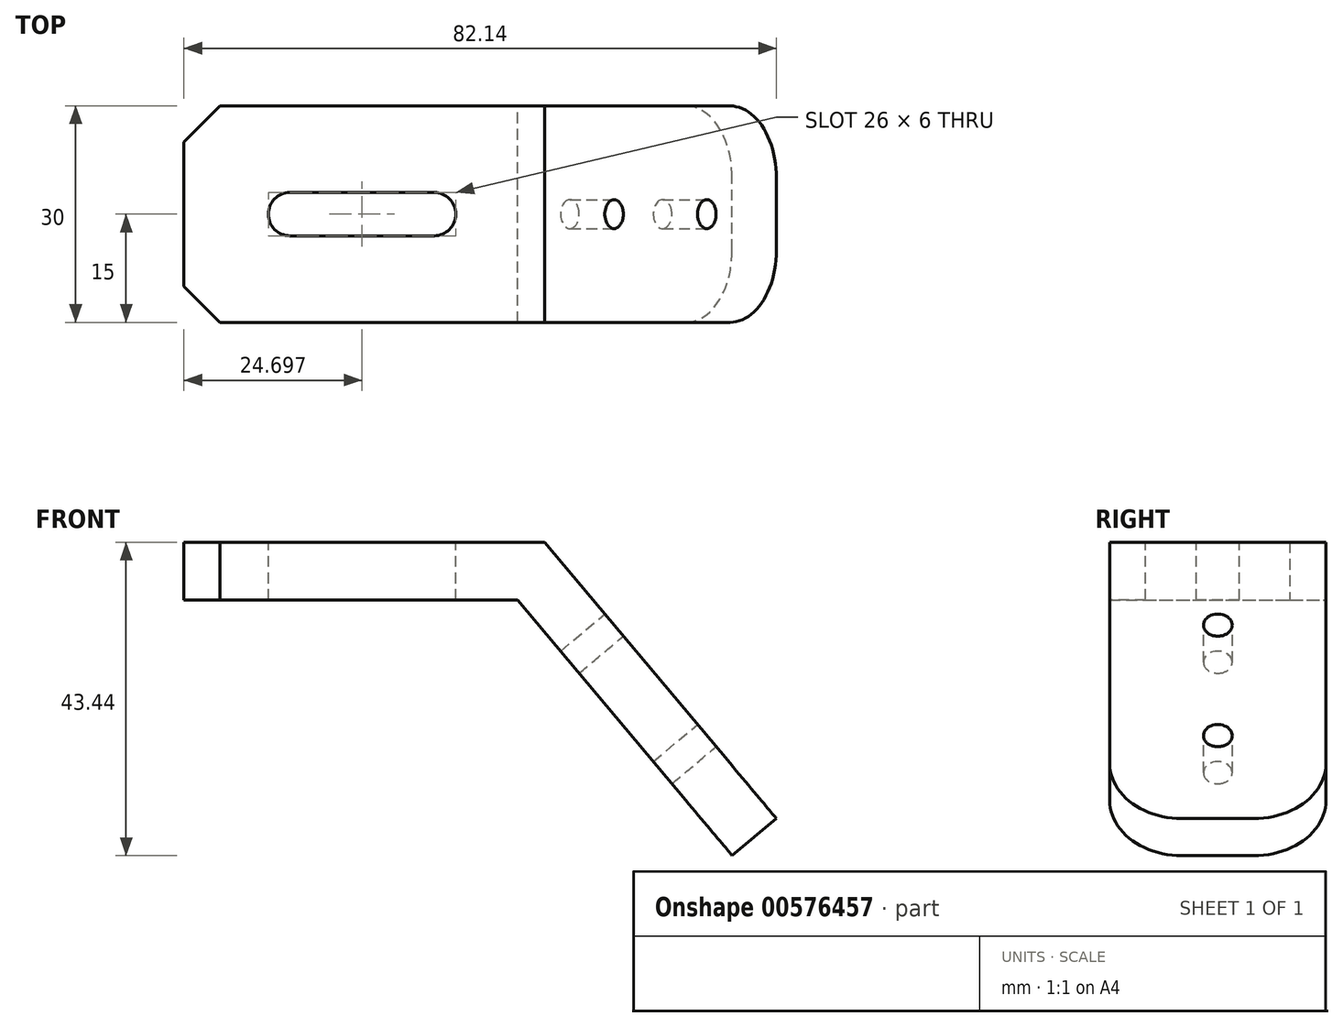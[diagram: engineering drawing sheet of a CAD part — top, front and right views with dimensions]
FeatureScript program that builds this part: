
annotation { "Feature Type Name" : "Feature", "Feature Type Description" : "" }
export const myFeature = defineFeature(function(context is Context, id is Id, definition is map)
    precondition{}
    {
        {
            var Q0;
            Q0=qCreatedBy(makeId("Front.planeOp"),FACE);
            var sketch = newSketch(context, id + "F0", { "sketchPlane" : qUnion([Q0])});
            skLineSegment(sketch, "E0", {"start": v(0, 0) * mm, "end": v(46.27, 0) * mm});
            skLineSegment(sketch, "E1", {"start": v(46.27, 0) * mm, "end": v(76.01, -35.44) * mm});
            skLineSegment(sketch, "E2.0", {"start": v(50, 8) * mm, "end": v(82.14, -30.3) * mm});
            skLineSegment(sketch, "E2.1", {"start": v(0, 8) * mm, "end": v(50, 8) * mm});
            skLineSegment(sketch, "E3", {"start": v(0, 0) * mm, "end": v(0, 8) * mm});
            skLineSegment(sketch, "E4", {"start": v(76.01, -35.44) * mm, "end": v(82.14, -30.3) * mm});
            skSolve(sketch);
        }
        {
            var Q0;
            Q0 = qSketchRegion(id + "F0", true);
            extrude(context, id + "F1", {"entities" : qUnion([Q0]), "endBound" : BoundingType.SYMMETRIC, "depth" : 30 * mm, "offsetDistance" : 25 * mm});
        }
        {
            var Q0;
            Q0=makeQuery(id+"F1.opExtrude","SWEPT_FACE",FACE,{"disambiguationData":[OSD([sQuery(id+"F0.wireOp",EDGE,"E2.1")])]});
            var sketch = newSketch(context, id + "F2", { "sketchPlane" : qUnion([Q0])});
            skLineSegment(sketch, "E5", {"start": v(14.7, 0) * mm, "end": v(34.7, 0) * mm});
            skArc(sketch, "E6.0.startCap", {"start": v(14.7, -3) * mm, "mid": v(11.7, 0) * mm, "end": v(14.7, 3) * mm});
            skArc(sketch, "E6.0.endCap", {"start": v(34.7, 3) * mm, "mid": v(37.7, 0) * mm, "end": v(34.7, -3) * mm});
            skLineSegment(sketch, "E6.0.left", {"start": v(14.7, 3) * mm, "end": v(34.7, 3) * mm});
            skLineSegment(sketch, "E6.0.right", {"start": v(14.7, -3) * mm, "end": v(34.7, -3) * mm});
            skSolve(sketch);
        }
        {
            var Q0;
            Q0 = qSketchRegion(id + "F2", true);
            extrude(context, id + "F3", {"entities" : qUnion([Q0]), "operationType" : NewBodyOperationType.REMOVE, "endBound" : BoundingType.THROUGH_ALL, "oppositeDirection" : true, "depth" : 25 * mm, "offsetDistance" : 25 * mm});
        }
        {
            var Q0;
            Q0=makeQuery(id+"F1.opExtrude","SWEPT_FACE",FACE,{"disambiguationData":[OSD([sQuery(id+"F0.wireOp",EDGE,"E2.0")])]});
            var sketch = newSketch(context, id + "F4", { "sketchPlane" : qUnion([Q0])});
            skPoint(sketch, "E7", {"position": v(0, -41.01) * mm});
            skPoint(sketch, "E8", {"position": v(0, -61.01) * mm});
            skSolve(sketch);
        }
        {
            var Q0;
            Q0=sQuery(id+"F4.wireOp",VERTEX,"E7");
            var Q1;
            Q1=sQuery(id+"F4.wireOp",VERTEX,"E8");
            var Q2;
            Q2=makeQuery(id+"F1.opExtrude","SWEPT_BODY",BODY,{"disambiguationData":[OSD([sQuery(id+"F0.wireOp",EDGE,"E0"),sQuery(id+"F0.wireOp",EDGE,"E1"),sQuery(id+"F0.wireOp",EDGE,"E2.0"),sQuery(id+"F0.wireOp",EDGE,"E2.1"),sQuery(id+"F0.wireOp",EDGE,"E3"),sQuery(id+"F0.wireOp",EDGE,"E4")])]});
            hole(context, id + "F5", {"style" : HoleStyle.SIMPLE, "endStyle" : HoleEndStyle.THROUGH, "holeDiameter" : 4 * mm, "majorDiameter" : 5 * mm, "isTappedThrough" : true, "tappedDepth" : 12 * mm, "tapClearance" : 3, "locations" : qUnion([Q0, Q1]), "scope" : qUnion([Q2])});
        }
        {
            var Q0;
            Q0=makeQuery(id+"F1.opExtrude","CAP_EDGE",EDGE,{"disambiguationData":[OSD([sQuery(id+"F0.wireOp",EDGE,"E4")])],"isStart":false});
            var Q1;
            Q1=makeQuery(id+"F1.opExtrude","CAP_EDGE",EDGE,{"disambiguationData":[OSD([sQuery(id+"F0.wireOp",EDGE,"E4")])],"isStart":true});
            fillet(context, id + "F6", {"entities" : qUnion([Q0, Q1]), "radius" : 10 * mm, "tangentPropagation" : true, "allowEdgeOverflow" : false});
        }
        {
            var Q0;
            Q0=makeQuery(id+"F1.opExtrude","CAP_EDGE",EDGE,{"disambiguationData":[OSD([sQuery(id+"F0.wireOp",EDGE,"E3")])],"isStart":true});
            var Q1;
            Q1=makeQuery(id+"F1.opExtrude","CAP_EDGE",EDGE,{"disambiguationData":[OSD([sQuery(id+"F0.wireOp",EDGE,"E3")])],"isStart":false});
            chamfer(context, id + "F7", {"entities" : qUnion([Q0, Q1]), "width" : 5 * mm, "tangentPropagation" : true});
        }
    });
